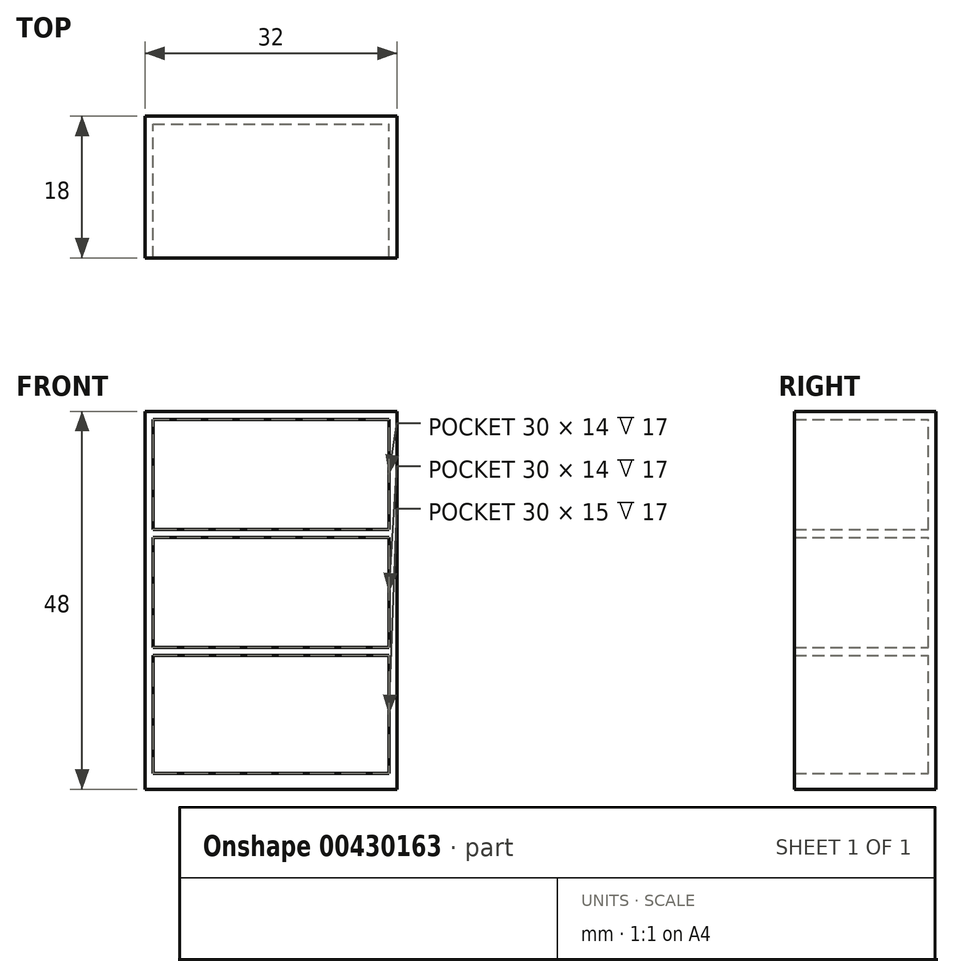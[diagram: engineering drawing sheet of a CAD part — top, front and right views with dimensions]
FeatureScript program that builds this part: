
annotation { "Feature Type Name" : "Feature", "Feature Type Description" : "" }
export const myFeature = defineFeature(function(context is Context, id is Id, definition is map)
    precondition{}
    {
        {
            var Q0;
            Q0=qCreatedBy(makeId("Front.planeOp"),FACE);
            var sketch = newSketch(context, id + "F0", { "sketchPlane" : qUnion([Q0])});
            skLineSegment(sketch, "E0.bottom", {"start": v(0, 0) * mm, "end": v(32, 0) * mm});
            skLineSegment(sketch, "E0.top", {"start": v(0, 48) * mm, "end": v(32, 48) * mm});
            skLineSegment(sketch, "E0.left", {"start": v(0, 0) * mm, "end": v(0, 48) * mm});
            skLineSegment(sketch, "E0.right", {"start": v(32, 0) * mm, "end": v(32, 48) * mm});
            skLineSegment(sketch, "E1.0", {"start": v(1, 47) * mm, "end": v(31, 47) * mm});
            skLineSegment(sketch, "E2.0", {"start": v(31, 2) * mm, "end": v(31, 17) * mm});
            skLineSegment(sketch, "E3.0", {"start": v(1, 2) * mm, "end": v(31, 2) * mm});
            skLineSegment(sketch, "E4.0", {"start": v(1, 2) * mm, "end": v(1, 17) * mm});
            skLineSegment(sketch, "E5.bottom", {"start": v(1, 32) * mm, "end": v(31, 32) * mm});
            skLineSegment(sketch, "E5.top", {"start": v(1, 33) * mm, "end": v(31, 33) * mm});
            skLineSegment(sketch, "E6.bottom", {"start": v(1, 18) * mm, "end": v(31, 18) * mm});
            skLineSegment(sketch, "E6.top", {"start": v(1, 17) * mm, "end": v(31, 17) * mm});
            skLineSegment(sketch, "E7.trimOffspring", {"start": v(31, 18) * mm, "end": v(31, 32) * mm});
            skLineSegment(sketch, "E8.trimOffspring", {"start": v(31, 33) * mm, "end": v(31, 47) * mm});
            skLineSegment(sketch, "E9.trimOffspring", {"start": v(1, 18) * mm, "end": v(1, 32) * mm});
            skLineSegment(sketch, "E10.trimOffspring", {"start": v(1, 33) * mm, "end": v(1, 47) * mm});
            skSolve(sketch);
        }
        {
            var Q0;
            Q0 = qSketchRegion(id + "F0", true);
            extrude(context, id + "F1", {"entities" : qUnion([Q0]), "depth" : 17 * mm});
        }
        {
            var Q0;
            Q0=qCreatedBy(makeId("Front.planeOp"),FACE);
            var sketch = newSketch(context, id + "F2", { "sketchPlane" : qUnion([Q0])});
            skLineSegment(sketch, "E11.bottom", {"start": v(32, 48) * mm, "end": v(0, 48) * mm});
            skLineSegment(sketch, "E11.top", {"start": v(32, 0) * mm, "end": v(0, 0) * mm});
            skLineSegment(sketch, "E11.left", {"start": v(32, 48) * mm, "end": v(32, 0) * mm});
            skLineSegment(sketch, "E11.right", {"start": v(0, 48) * mm, "end": v(0, 0) * mm});
            skSolve(sketch);
        }
        {
            var Q0;
            Q0 = qSketchRegion(id + "F2", true);
            extrude(context, id + "F3", {"entities" : qUnion([Q0]), "operationType" : NewBodyOperationType.ADD, "oppositeDirection" : true, "depth" : 1 * mm});
        }
    });
